# Revit family: 3-HC_RAS_HCL_TOSHIBA_TCTC_PAVSG_10-22
name_source: partatom
category: Mechanical Equipment
revit_build: Autodesk Revit 2017 (Build: 20160225_1515(x64)
units: mm (PartAtom-declared; Revit-internal decimal feet)

## family parameters
Always vertical = Yes
Cut with Voids When Loaded = No
OmniClass Number = 23.75.00.00
OmniClass Title = Climate Control (HVAC)
Part Type = Normal
Room Calculation Point = No
Round Connector Dimension = Use Diameter
Shared = No
Work Plane-Based = No

## types (11) — shared parameters
Compressor detail - Type = Hermetic twin rotary compressor
Content Supplier URL = www.hcltech.com
Custom = No
Depth (mm) = 290 mm  [stored 0.951444 ft]
EMCS = 4
ETIM Article Class = EC001213
Frequency (Hz) = 50Hz 220-240V
Height (mm) = 550 mm  [stored 1.80446 ft]
MEPcontent Class = HEATPUMP
Manufacturer = Toshiba
Manufacturer URL = https://www.toshiba-carrier.co.jp
Product Line = TCTC
Red = Colour RGB-250 000 000
URL = https://www.toshiba-carrier.co.jp
White = Colour RGB-255 255 255
Width (mm) = 780 mm  [stored 2.55906 ft]

## per-type parameters (varying)
| type | Airflow | Article Description | Capacities - Cooling (kW) | Capacities - Heating (kW) | Compressor detail - Motor output  (kW) | Description | Hydronic Return Diameter (mm) | Hydronic Supply Diameter (mm) | MOCP (A) | Maximum current A | Operating range - Cooling (°C) | Operating range - Heating (°C) | Power consumption-Cooling (Kw) | Power consumption-Heating (Kw) | Refrigerant information | Running current-Cooling (A) | Running current-Heating (A) | Sound pressure - Cooling (dB) | Sound pressure - Heating (dB) | Voltage (V) | Weight (Kg) |
| RAV-GM301ATP-E | 1800 | R32 DI S4 1Ph/3PH | 2.5 | 3.4 | 0.75 | R32 DI S4 1Ph/3PH | 10 mm  [stored 0.0328084 ft] | 6 mm  [stored 0.019685 ft] | 15 | 7.9 | -15 to 46 degC | -15to 15 degC | 0.61 | 0.85 | R32 | 3.07 - 2.83 | 4.17 - 3.80 | 46 | 47 | 60Hz 220V | 29 |
| RAV-GM401ATP-E | 2200 | R32 DI S4 1Ph/3PH | 3.6 | 4.0 | 1.1 | R32 DI S4 1Ph/3PH | 13 mm | 6 mm  [stored 0.019685 ft] | 15 | 9.2 | -15 to 46 degC | -15to 15 degC | 1.13 | 1.12 | R32 | 5.60 - 5.10 | 5.50 - 6.00 | 49 | 50 | 60Hz 220V | 34 |
| RAV-GM561ATP-E | 2400 | R32 DI S4 1Ph/3PH | 5.0 | 5.3 | 1.1 | R32 DI S4 1Ph/3PH | 13 mm | 6 mm  [stored 0.019685 ft] | 20 | 15.5 | -15 to 46 degC | -15to 15 degC | 1.66 | 1.55 | R32 | 7.78 - 7.13 | 7.26 - 6.66 | 46 | 48 | 60Hz 220V | 40 |
| RAV-GM801ATP-E | 2700 | R32 DI S4 1Ph/3PH | 6.7 | 7.7 | 1.6 | R32 DI S4 1Ph/3PH | 16 mm | 10 mm  [stored 0.0328084 ft] | 20 | 15.5 | -15 to 46 degC | -15to 15 degC | 2.44 | 2.81 | R32 | 11.43 - 1-.48 | 12.23 - 11.21 | 48 | 52 | 60Hz 220V | 43 |
| RAV-SP404ATP-E | 2400 | R410A SDI S4 1Ph/3PH | 3.6 | 4.0 | 1.1 | R410A SDI S4 1Ph/3PH | 13 mm | 6 mm  [stored 0.019685 ft] | 16 | 15 | -15 to 43 degC | -15to 15 degC | 1.07 | 1.04 | R410A | 5.40 - 4.95 | 5.13 - 4.70 | 45 | 47 |  | 40 |
| RAV-SP454ATP-E | 2400 | R410A SDI S4 1Ph/3PH | 4.0 | 4.5 | 1.1 | R410A SDI S4 1Ph/3PH | 13 mm | 6 mm  [stored 0.019685 ft] | 16 | 15 | -15 to 43 degC | -15to 15 degC | 1.23 | 1.24 | R410A | 6.01 - 5.50 | 6.06 - 5.55 | 45 | 47 |  | 40 |
| RAV-SP564ATP-E | 2400 | R410A SDI S4 1Ph/3PH | 5.0 | 5.6 | 1.1 | R410A SDI S4 1Ph/3PH | 13 mm | 6 mm  [stored 0.019685 ft] | 16 | 15 | -15 to 43 degC | -20 to 15 degC | 1.56 | 1.55 | R410A | 7.23 - 6.62 | 7.18 - 6.58 | 47 | 48 |  | 40 |
| RAV-SM304ATP-E | 1800 | R410A DI S4 1Ph/3PH | 2.5 | 3.4 | 0.75 | R410A DI S4 1Ph/3PH | 10 mm  [stored 0.0328084 ft] | 6 mm  [stored 0.019685 ft] | 11 | 8.5 | -15 to 46 degC | -15 to 24 degC | 0.61 | 0.85 | R410A |  |  | 46 | 47 | 60Hz 220V | 33 |
| RAV-SM404ATP-E | 2220 | R410A DI S4 1Ph/3PH | 3.6 | 4.0 | 1.1 | R410A DI S4 1Ph/3PH | 13 mm | 6 mm  [stored 0.019685 ft] | 12 | 10 | -15 to 46 degC | -15 to 24 degC | 1.13 | 1.12 | R410A |  |  | 49 | 50 | 60Hz 220V | 39 |
| RAV-SM564ATP-E | 2400 | R410A DI S4 1Ph/3PH | 5.0 | 5.3 | 1.1 | R410A DI S4 1Ph/3PH | 13 mm | 6 mm  [stored 0.019685 ft] | 20 | 15.5 | -15 to 46 degC | -15 to 15 degC | 1.83 | 1.62 | R410A | 8.58 - 7.86 | 7.59 - 6.96 | 46 | 48 | 60Hz 220V | 40 |
| RAV-SM804ATP-E | 2700 | R410A DI S4 1Ph/3PH | 6.7 | 7.7 | 1.6 | R410A DI S4 1Ph/3PH | 16 mm | 10 mm  [stored 0.0328084 ft] | 20 | 15.5 | -15 to 46 degC | -15 to 15 degC | 2.38 | 2.32 | R410A | 11.15 - 10.22 | 10.87 - 9.97 | 48 | 52 | 60Hz 220V | 44 |

note: column(s) folded — value = type name in every type: Article Type, Manufacturer Art. No., Model

note: [stored X ft] marks values corroborated as IEEE doubles in the binary element streams (Revit-internal decimal feet)

## geometry (parser evidence)
native form markers: Sweep x3
no freeform markers — native parametric forms only
